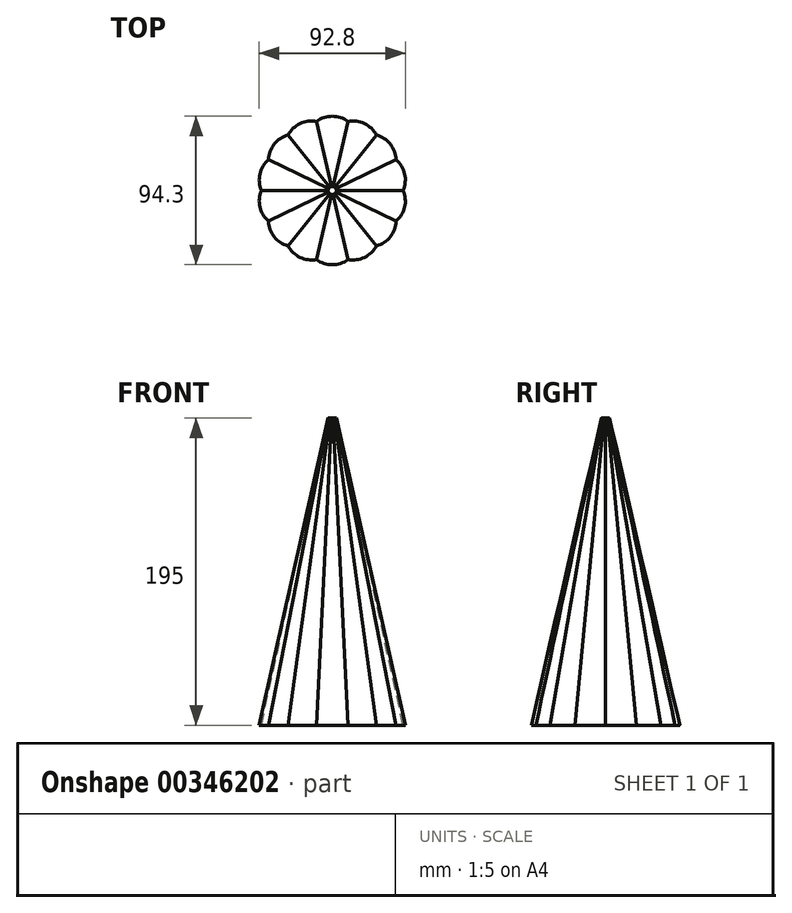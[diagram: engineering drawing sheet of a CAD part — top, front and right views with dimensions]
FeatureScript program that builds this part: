
annotation { "Feature Type Name" : "Feature", "Feature Type Description" : "" }
export const myFeature = defineFeature(function(context is Context, id is Id, definition is map)
    precondition{}
    {
        {
            var Q0;
            Q0=qCreatedBy(makeId("Top.planeOp"),FACE);
            var sketch = newSketch(context, id + "F0", { "sketchPlane" : qUnion([Q0])});
            skCircle(sketch, "E0", {"center": v(0, 0) * mm, "radius": 45 * mm, "construction": true});
            skArc(sketch, "E1", {"start": v(10.05, 43.86) * mm, "mid": v(0, 47.15) * mm, "end": v(-10.05, 43.86) * mm});
            skArc(sketch, "E2.1.0", {"start": v(-9.98, 43.88) * mm, "mid": v(-20.46, 42.48) * mm, "end": v(-28.09, 35.16) * mm});
            skArc(sketch, "E2.2.0", {"start": v(-28.03, 35.2) * mm, "mid": v(-36.87, 29.4) * mm, "end": v(-40.56, 19.5) * mm});
            skArc(sketch, "E2.3.0", {"start": v(-40.53, 19.56) * mm, "mid": v(-45.97, 10.5) * mm, "end": v(-45, -0.04) * mm});
            skArc(sketch, "E2.4.0", {"start": v(-45, 0.04) * mm, "mid": v(-45.97, -10.5) * mm, "end": v(-40.53, -19.56) * mm});
            skArc(sketch, "E2.5.0", {"start": v(-40.56, -19.5) * mm, "mid": v(-36.87, -29.4) * mm, "end": v(-28.03, -35.2) * mm});
            skArc(sketch, "E2.6.0", {"start": v(-28.09, -35.16) * mm, "mid": v(-20.46, -42.48) * mm, "end": v(-9.98, -43.88) * mm});
            skArc(sketch, "E2.7.0", {"start": v(-10.05, -43.86) * mm, "mid": v(0, -47.15) * mm, "end": v(10.05, -43.86) * mm});
            skArc(sketch, "E2.8.0", {"start": v(9.98, -43.88) * mm, "mid": v(20.46, -42.48) * mm, "end": v(28.09, -35.16) * mm});
            skArc(sketch, "E2.9.0", {"start": v(28.03, -35.2) * mm, "mid": v(36.87, -29.4) * mm, "end": v(40.56, -19.5) * mm});
            skArc(sketch, "E2.10.0", {"start": v(40.53, -19.56) * mm, "mid": v(45.97, -10.5) * mm, "end": v(45, 0.04) * mm});
            skArc(sketch, "E2.11.0", {"start": v(45, -0.04) * mm, "mid": v(45.97, 10.5) * mm, "end": v(40.53, 19.56) * mm});
            skArc(sketch, "E2.12.0", {"start": v(40.56, 19.5) * mm, "mid": v(36.87, 29.4) * mm, "end": v(28.03, 35.2) * mm});
            skArc(sketch, "E2.13.0", {"start": v(28.09, 35.16) * mm, "mid": v(20.46, 42.48) * mm, "end": v(9.98, 43.88) * mm});
            skSolve(sketch);
        }
        {
            var Q0;
            Q0=qCreatedBy(makeId("Top.planeOp"),FACE);
            cPlane(context, id + "F1", {"entities" : qUnion([Q0]), "cplaneType" : CPlaneType.OFFSET, "offset" : 195 * mm, "width" : 150 * mm, "height" : 150 * mm});
        }
        {
            var Q0;
            Q0=qCreatedBy(id+"F1.planeOp",FACE);
            var sketch = newSketch(context, id + "F2", { "sketchPlane" : qUnion([Q0])});
            skCircle(sketch, "E3", {"center": v(0, 0) * mm, "radius": 2.5 * mm, "construction": true});
            skArc(sketch, "E4", {"start": v(0.56, 2.44) * mm, "mid": v(0, 2.6) * mm, "end": v(-0.56, 2.44) * mm});
            skArc(sketch, "E5.1.0", {"start": v(-0.55, 2.44) * mm, "mid": v(-1.13, 2.35) * mm, "end": v(-1.56, 1.95) * mm});
            skArc(sketch, "E5.2.0", {"start": v(-1.56, 1.96) * mm, "mid": v(-2.04, 1.63) * mm, "end": v(-2.25, 1.08) * mm});
            skArc(sketch, "E5.3.0", {"start": v(-2.25, 1.09) * mm, "mid": v(-2.54, 0.58) * mm, "end": v(-2.5, 0) * mm});
            skArc(sketch, "E5.4.0", {"start": v(-2.5, 0) * mm, "mid": v(-2.54, -0.58) * mm, "end": v(-2.25, -1.09) * mm});
            skArc(sketch, "E5.5.0", {"start": v(-2.25, -1.08) * mm, "mid": v(-2.04, -1.63) * mm, "end": v(-1.56, -1.96) * mm});
            skArc(sketch, "E5.6.0", {"start": v(-1.56, -1.95) * mm, "mid": v(-1.13, -2.35) * mm, "end": v(-0.55, -2.44) * mm});
            skArc(sketch, "E5.7.0", {"start": v(-0.56, -2.44) * mm, "mid": v(0, -2.6) * mm, "end": v(0.56, -2.44) * mm});
            skArc(sketch, "E5.8.0", {"start": v(0.55, -2.44) * mm, "mid": v(1.13, -2.35) * mm, "end": v(1.56, -1.95) * mm});
            skArc(sketch, "E5.9.0", {"start": v(1.56, -1.96) * mm, "mid": v(2.04, -1.63) * mm, "end": v(2.25, -1.08) * mm});
            skArc(sketch, "E5.10.0", {"start": v(2.25, -1.09) * mm, "mid": v(2.54, -0.58) * mm, "end": v(2.5, 0) * mm});
            skArc(sketch, "E5.11.0", {"start": v(2.5, 0) * mm, "mid": v(2.54, 0.58) * mm, "end": v(2.25, 1.09) * mm});
            skArc(sketch, "E5.12.0", {"start": v(2.25, 1.08) * mm, "mid": v(2.04, 1.63) * mm, "end": v(1.56, 1.96) * mm});
            skArc(sketch, "E5.13.0", {"start": v(1.56, 1.95) * mm, "mid": v(1.13, 2.35) * mm, "end": v(0.55, 2.44) * mm});
            skSolve(sketch);
        }
        {
            var Q0;
            {var subQ15=sQuery(id+"F0.wireOp",EDGE,"E2.1.0");var subQ16=sQuery(id+"F0.wireOp",EDGE,"E1");var subQ17=makeQuery(id+"F0.imprint","INTERSECT",VERTEX,{"derivedFrom":[subQ16,subQ15]});Q0=makeQuery(id+"F0.imprint","IMPRINT",FACE,{"disambiguationData":[TD([[makeQuery(id+"F0.imprint","IMPRINT",EDGE,{"disambiguationData":[TD([[subQ17,1.0]])],"derivedFrom":subQ16}),1.0]])]});}
            var Q1;
            {var subQ15=sQuery(id+"F2.wireOp",EDGE,"E5.1.0");var subQ16=sQuery(id+"F2.wireOp",EDGE,"E4");var subQ17=makeQuery(id+"F2.imprint","INTERSECT",VERTEX,{"derivedFrom":[subQ16,subQ15]});Q1=makeQuery(id+"F2.imprint","IMPRINT",FACE,{"disambiguationData":[TD([[makeQuery(id+"F2.imprint","IMPRINT",EDGE,{"disambiguationData":[TD([[subQ17,1.0]])],"derivedFrom":subQ16}),1.0]])]});}
            loft(context, id + "F3", {"sheetProfilesArray" : [{ "sheetProfileEntities" : qUnion([Q0]) }, { "sheetProfileEntities" : qUnion([Q1]) }]});
        }
    });
